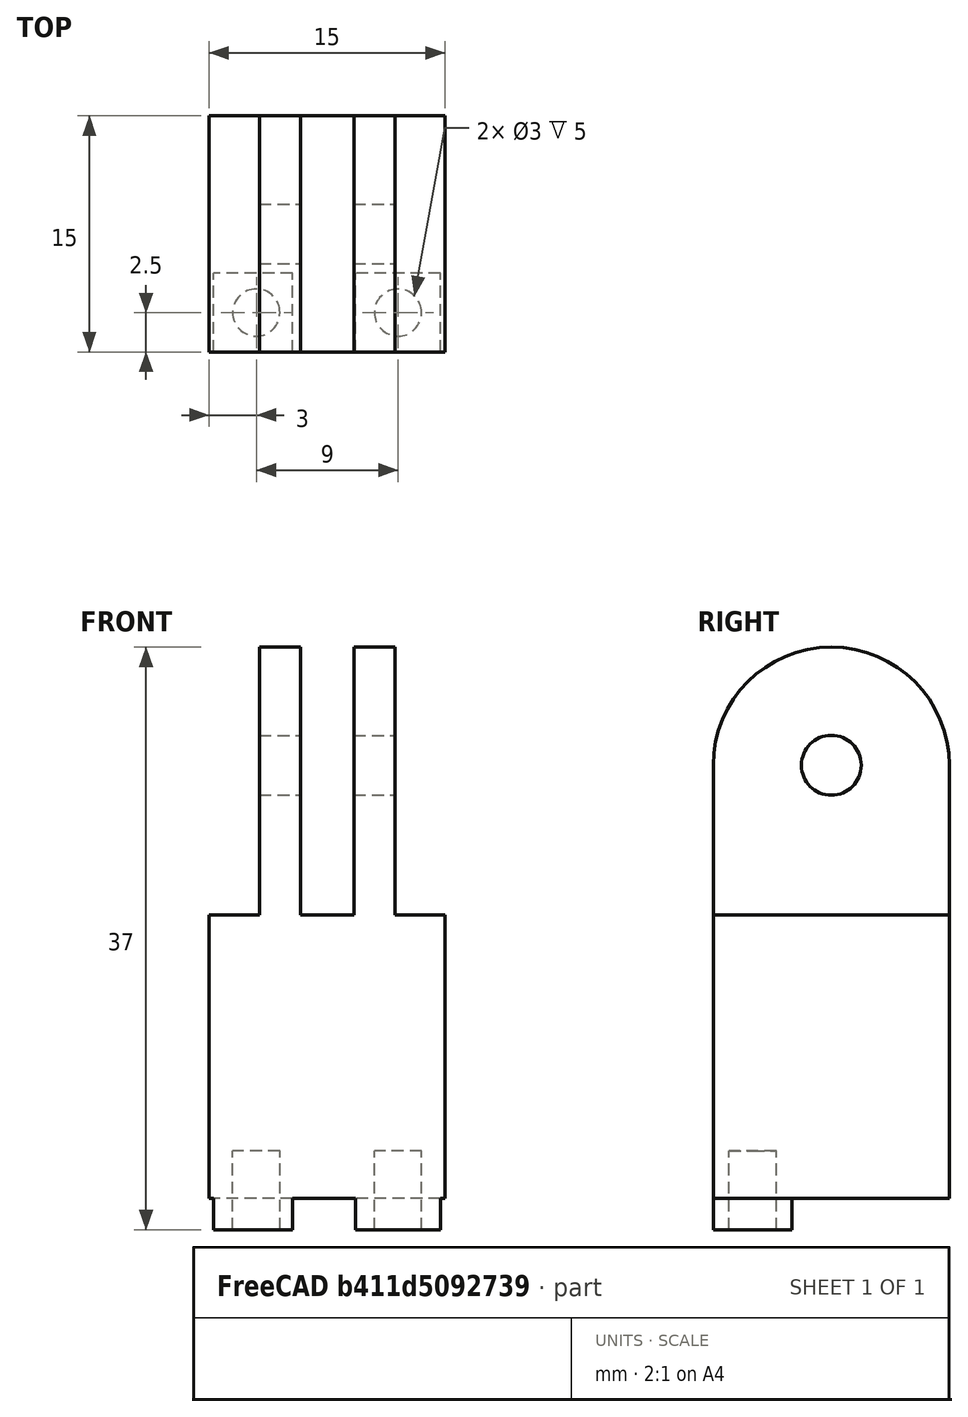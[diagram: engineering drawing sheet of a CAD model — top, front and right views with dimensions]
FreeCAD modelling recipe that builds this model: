
FCSTD DOCUMENT  (FreeCAD 0.18.4R)
Label: 9960sensor
License: FreeArt
LicenseURL: http://artlibre.org/licence/lal
objects: Part::Box×3, Part::MultiFuse×2, Spreadsheet::Sheet×1, Part::Cylinder×1, Part::FeaturePython×1, Part::Feature×1, Part::Cut×1, App::Part×1
note: 9 computed .brp shape members not serialized (recipe doc carries the construction recipe); baked Part::Feature solids carry a one-line shape summary decoded from their .brp

FEATURE [Part::Box] Box  label="base cube"
  AttacherType = Attacher::AttachEngine3D
  Height = 5
  Length = 14.4
  Placement = pos=(0.3,0,0) rot=(0,0,1;0rad)
  Width = 5
  expr: Placement.Base.x = (p.stick_width - p.pcb_x) / 2
  expr: Height = p.pcb_back + p.wall
  expr: Width = p.stand_y
  expr: Length = p.pcb_x
FEATURE [Spreadsheet::Sheet] Spreadsheet  label="p"
  cells = A1=pcb_x; B1(pcb_x)=14.4; A2=pcb_y; B2(pcb_y)=13.6; A3=pcb_z; B3(pcb_z)=1.8; A4=pcb_fwd; B4(pcb_fwd)=2; A5=pcb_back; B5(pcb_back)=2; A6=stand_x; B6(stand_x)=5; A7=stand_y; B7(stand_y)=5; A8=hole_dist_x; B8(hole_dist_x)=9; A9=hole_off_y; B9(hole_off_y)=2.5; A10=hole_r; B10(hole_r)=1.5; A11=sensor_hole_x; B11(sensor_hole_x)=2.6; A12=sensor_hole_y; B12(sensor_hole_y)=4.5; A13=wall; B13(wall)=3; A14=stick_width; B14(stick_width)=15; A15=stick_length; B15(stick_length)=15
FEATURE [Part::Cylinder] Cylinder  label="bolt hole"
  Angle = 360
  AttacherType = Attacher::AttachEngine3D
  Height = 5
  Radius = 1.5
  expr: Height = p.pcb_back + p.wall
  expr: Radius = p.hole_r
FEATURE [Part::FeaturePython] Array  label="bolt hole array"  # Draft array (typed FeaturePython)
  Angle = 360
  ArrayType = 0
  Axis = (0,0,1)
  Base = -> Cylinder
  Center = (0,0,0)
  Fuse = false
  IntervalAxis = (0,0,0)
  IntervalX = (9,0,0)
  IntervalY = (0,1,0)
  IntervalZ = (0,0,1)
  NumberPolar = 1
  NumberX = 2
  NumberY = 1
  NumberZ = 1
  Placement = pos=(2.7,2.5,0) rot=(0,0,1;0rad)
  expr: Placement.Base.y = p.stand_y / 2
  expr: Placement.Base.x = (p.pcb_x - p.hole_dist_x) / 2
  expr: IntervalX.x = p.hole_dist_x
FEATURE [Part::Box] Box001  label="base extract cube"
  AttacherType = Attacher::AttachEngine3D
  Height = 2
  Length = 4
  Placement = pos=(5,0,0) rot=(0,0,1;0rad)
  Width = 5
  expr: Width = p.stand_y
  expr: Height = p.pcb_back
  expr: Placement.Base.x = p.stand_x
  expr: Length = p.hole_dist_x - p.stand_x
FEATURE [Part::Box] Box002  label="stick cube"
  AttacherType = Attacher::AttachEngine3D
  Height = 15
  Length = 15
  Placement = pos=(0,0,2) rot=(0,0,1;0rad)
  Width = 15
  expr: Height = p.stick_length
  expr: Placement.Base.z = p.pcb_back
  expr: Width = p.stick_width
  expr: Length = p.stick_width
FEATURE [Part::Feature] Cut001001  label="side 2 cut001"
  Placement = pos=(7.5,7.5,17) rot=(0,0,1;1.5708rad)
  shape: bbox 15 x 15 x 20 mm, 16 faces (baked)
  expr: Placement.Base.z = p.pcb_back + p.stick_length
  expr: Placement.Base.x = p.stick_width / 2
  expr: Placement.Base.y = p.stick_width / 2
FEATURE [Part::MultiFuse] Fusion  label="holder fusion"
  Shapes = -> [Box002,Cut001001,Box]
FEATURE [Part::MultiFuse] Fusion001  label="holder extract fusion"
  Placement = pos=(0.3,0,0) rot=(0,0,1;0rad)
  Shapes = -> [Array,Box001]
  expr: Placement.Base.x = (p.stick_width - p.pcb_x) / 2
FEATURE [Part::Cut] Cut  label="9960 sensor cut"
  Base = -> Fusion
  Tool = -> Fusion001
FEATURE [App::Part] Part  label="9960 sensor part"
  Group = -> [Cylinder,Array,Cut001001,Box001,Box002,Fusion,Fusion001,Cut]
  Origin = -> Origin
